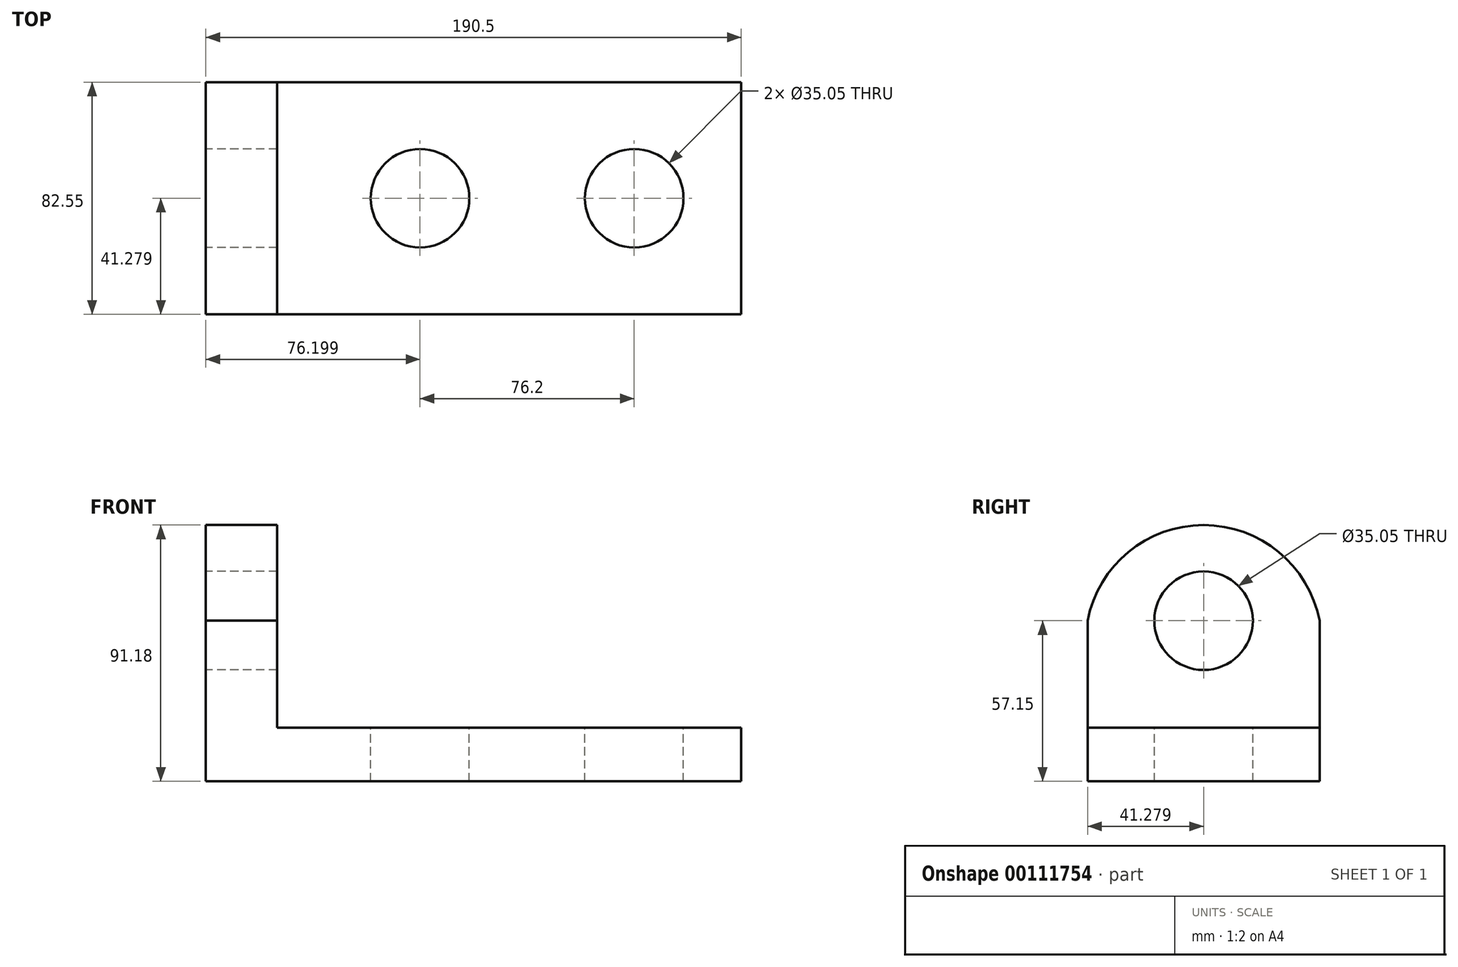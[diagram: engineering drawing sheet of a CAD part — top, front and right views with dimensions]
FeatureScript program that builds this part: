
annotation { "Feature Type Name" : "Feature", "Feature Type Description" : "" }
export const myFeature = defineFeature(function(context is Context, id is Id, definition is map)
    precondition{}
    {
        {
            var Q0;
            Q0=qCreatedBy(makeId("Top.planeOp"),FACE);
            var sketch = newSketch(context, id + "F0", { "sketchPlane" : qUnion([Q0])});
            skLineSegment(sketch, "E0.bottom", {"start": v(-126.06, 51.11) * mm, "end": v(64.44, 51.11) * mm});
            skLineSegment(sketch, "E0.top", {"start": v(-126.06, -31.44) * mm, "end": v(64.44, -31.44) * mm});
            skLineSegment(sketch, "E0.left", {"start": v(-126.06, 51.11) * mm, "end": v(-126.06, -31.44) * mm});
            skLineSegment(sketch, "E0.right", {"start": v(64.44, 51.11) * mm, "end": v(64.44, -31.44) * mm});
            skCircle(sketch, "E1", {"center": v(26.34, 9.84) * mm, "radius": 17.53 * mm});
            skCircle(sketch, "E2", {"center": v(-49.86, 9.84) * mm, "radius": 17.53 * mm});
            skSolve(sketch);
        }
        {
            var Q0;
            Q0 = qSketchRegion(id + "F0", true);
            extrude(context, id + "F1", {"entities" : qUnion([Q0]), "oppositeDirection" : true, "depth" : 19.05 * mm});
        }
        {
            var Q0;
            Q0=makeQuery(id+"F1.opExtrude","SWEPT_FACE",FACE,{"disambiguationData":[OSD([sQuery(id+"F0.wireOp",EDGE,"E0.left")])]});
            var sketch = newSketch(context, id + "F2", { "sketchPlane" : qUnion([Q0])});
            skLineSegment(sketch, "E3.bottom", {"start": v(-51.11, -19.05) * mm, "end": v(31.44, -19.05) * mm});
            skLineSegment(sketch, "E3.top", {"start": v(-51.11, 38.1) * mm, "end": v(31.44, 38.1) * mm});
            skLineSegment(sketch, "E3.left", {"start": v(-51.11, -19.05) * mm, "end": v(-51.11, 38.1) * mm});
            skLineSegment(sketch, "E3.right", {"start": v(31.44, -19.05) * mm, "end": v(31.44, 38.1) * mm});
            skArc(sketch, "E4", {"start": v(31.44, 38.1) * mm, "mid": v(-9.84, 72.13) * mm, "end": v(-51.11, 38.1) * mm});
            skSolve(sketch);
        }
        {
            var Q0;
            Q0 = qSketchRegion(id + "F2", true);
            extrude(context, id + "F3", {"entities" : qUnion([Q0]), "operationType" : NewBodyOperationType.ADD, "oppositeDirection" : true, "depth" : 25.4 * mm});
        }
        {
            var Q0;
            Q0=makeQuery(id+"F3.boolean.opBoolean","MERGE",FACE,{"derivedFrom":[makeQuery(id+"F1.opExtrude","SWEPT_FACE",FACE,{"disambiguationData":[OSD([sQuery(id+"F0.wireOp",EDGE,"E0.left")])]}),makeQuery(id+"F3.opExtrude","CAP_FACE",FACE,{"disambiguationData":[OSD([sQuery(id+"F2.wireOp",EDGE,"E3.bottom"),sQuery(id+"F2.wireOp",EDGE,"E3.left"),sQuery(id+"F2.wireOp",EDGE,"E3.right"),sQuery(id+"F2.wireOp",EDGE,"E4")])],"isStart":true})]});
            var sketch = newSketch(context, id + "F4", { "sketchPlane" : qUnion([Q0])});
            skCircle(sketch, "E5", {"center": v(-9.84, 38.1) * mm, "radius": 17.53 * mm});
            skSolve(sketch);
        }
        {
            var Q0;
            Q0 = qSketchRegion(id + "F4", true);
            extrude(context, id + "F5", {"entities" : qUnion([Q0]), "operationType" : NewBodyOperationType.REMOVE, "oppositeDirection" : true, "depth" : 25.4 * mm});
        }
    });
